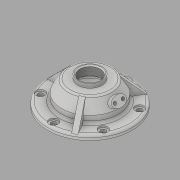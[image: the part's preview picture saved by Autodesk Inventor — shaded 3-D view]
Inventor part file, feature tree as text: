
AUTODESK INVENTOR PART (.ipt)
format: ipt  version: 2020 (Build 240168000, 168)  size: 345,088 bytes
history: native  units: mm
features: sketch x9, hole x4, thread x3, extrude x2, pattern_circular x2, plane x2, revolve x1
ambient origin geometry x8: Origin, YZ Plane, XZ Plane, XY Plane, X Axis, Y Axis, Z Axis, Center Point
bodies: Solid1 (feature_tree)
feature tree (23):
  revolve  "Revolution1"  [1 undecoded]
  extrude  "Extrusion1"  Depth=6.0mm
  hole  "Hole1"  [1 undecoded]
  hole  "Hole2"  [1 undecoded]
  pattern_circular  "Circular Pattern1"  Count=4  [1 undecoded]
  pattern_circular  "Circular Pattern2"  Angle=90.0deg  [1 undecoded]
  plane  "Work Plane1"
  sketch  "Sketch5"  dims[d9=11.0mm d10=40.0mm]
  sketch  "Sketch6"  dims[d11=30.0deg]
  plane  "Work Plane2"
  extrude  "Extrusion2"  Depth=2.0mm
  hole  "Hole3"  [1 undecoded]
  hole  "Hole4"  [1 undecoded]
  thread  "Thread1"  [1 undecoded]
  thread  "Thread2"  [1 undecoded]
  thread  "Thread3"  [1 undecoded]
  sketch  "Sketch1"  dims[d0=104.0mm d2=54.0mm]
  sketch  "Sketch2"  dims[d3=30.0mm d4=6.0mm]
  sketch  "Sketch3"  dims[d5=15.0mm d6=70.0mm]
  sketch  "Sketch4"  dims[d7=50.0mm d8=18.0mm]
  sketch  "Sketch7"  dims[d12=24.0mm]
  sketch  "Sketch8"  dims[d13=3.0mm]
  sketch  "Sketch9"  dims[d14=3.0mm d15=90.0deg d16=3.0mm d17=3.0mm d18=6.0mm d19=0.0mm d20=90.0mm d21=6.5mm d22=6.0mm d23=11.0mm d24=2.0mm d25=90.0deg d26=8.0mm d27=20.594885mm d28=90.0mm d29=4.0mm d30=6.0mm d31=11.0mm d32=2.0mm d33=90.0deg d34=8.0mm d35=20.594885mm d36=30.0mm d37=360.0deg d39=-1.5mm d40=5.0mm d41=0.0mm d43=12.0mm d44=18.0mm d45=10.0mm d46=4.0mm d47=6.0mm d48=4.0mm d49=2.0mm d50=90.0deg d51=8.0mm d52=20.594885mm d53=30.0mm d54=35.0mm d55=25.4mm d56=6.0mm d57=28.0mm d58=2.0mm d59=90.0deg d60=8.0mm d61=20.594885mm d62=60.0mm d63=360.0deg d65=9.7mm d66=0.0mm d67=5.0mm d68=0.0mm d69=5.0mm d70=0.0mm]
note: 10 required parameter values undecoded (feature->parameter linkage not recoverable at this tier; creation-order binding heuristic only, values carry confidence <= 0.55)